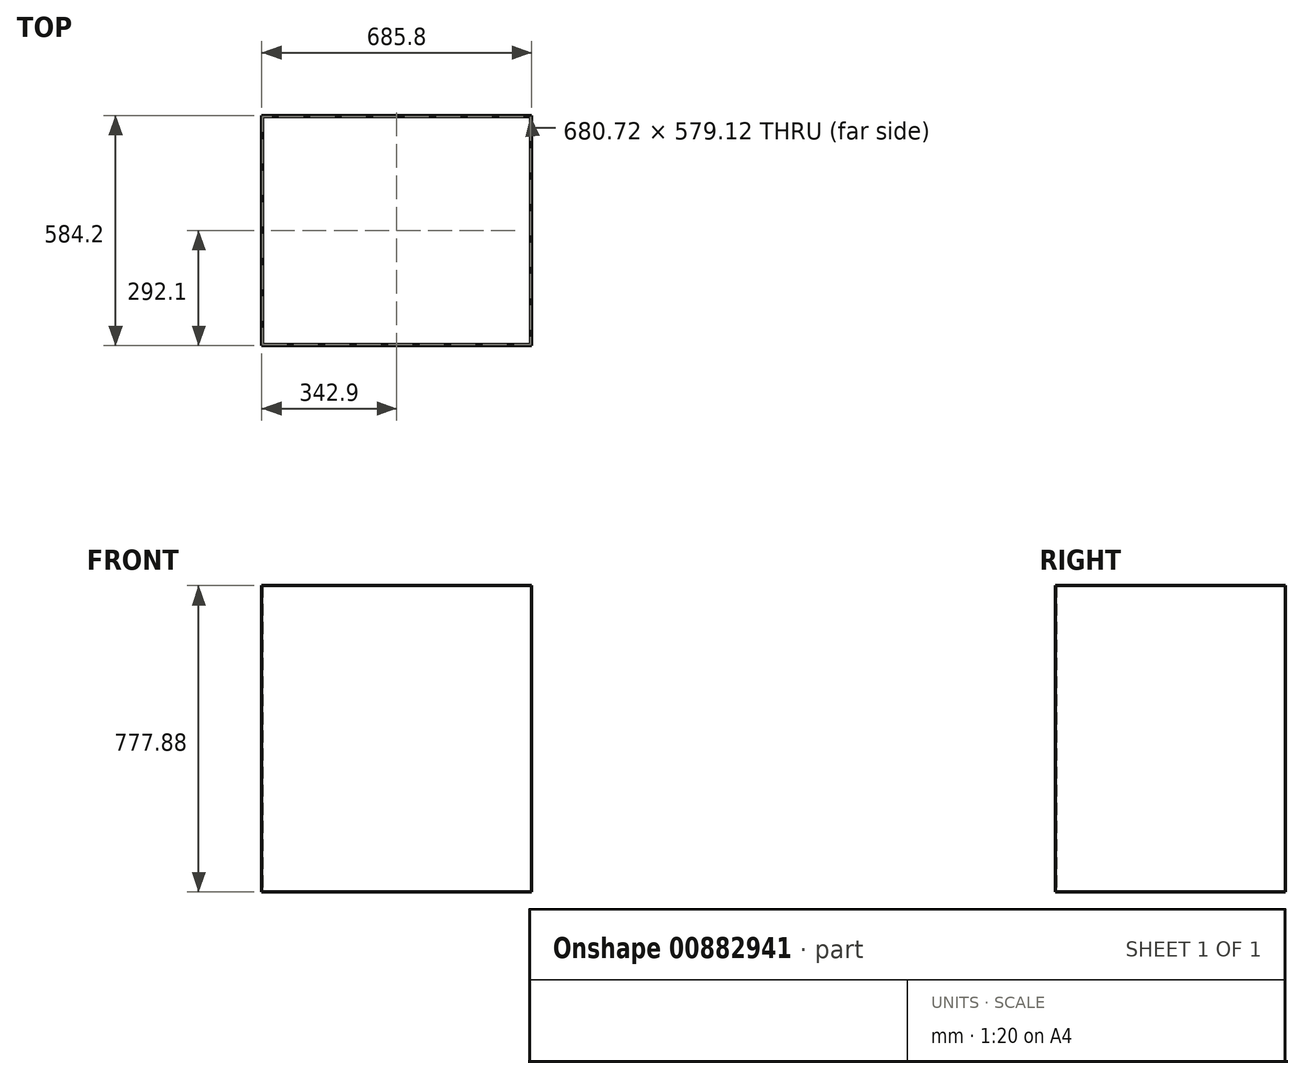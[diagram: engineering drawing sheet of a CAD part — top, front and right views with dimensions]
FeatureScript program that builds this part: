
annotation { "Feature Type Name" : "Feature", "Feature Type Description" : "" }
export const myFeature = defineFeature(function(context is Context, id is Id, definition is map)
    precondition{}
    {
        {
            var Q0;
            Q0=qCreatedBy(makeId("Top.planeOp"),FACE);
            var sketch = newSketch(context, id + "F0", { "sketchPlane" : qUnion([Q0])});
            skLineSegment(sketch, "E0.bottom", {"start": v(-342.9, 292.1) * mm, "end": v(342.9, 292.1) * mm});
            skLineSegment(sketch, "E0.top", {"start": v(-342.9, -292.1) * mm, "end": v(342.9, -292.1) * mm});
            skLineSegment(sketch, "E0.left", {"start": v(-342.9, 292.1) * mm, "end": v(-342.9, -292.1) * mm});
            skLineSegment(sketch, "E0.right", {"start": v(342.9, 292.1) * mm, "end": v(342.9, -292.1) * mm});
            skPoint(sketch, "E0.middle", {"position": v(0, 0) * mm});
            skSolve(sketch);
        }
        {
            var Q0;
            Q0=makeQuery(id+"F0.imprint","IMPRINT",FACE,{"disambiguationData":[TD([[makeQuery(id+"F0.imprint","IMPRINT",EDGE,{"derivedFrom":sQuery(id+"F0.wireOp",EDGE,"E0.bottom")}),-1.0]])]});
            extrude(context, id + "F1", {"entities" : qUnion([Q0]), "depth" : 777.88 * mm, "offsetDistance" : 25.4 * mm});
        }
        {
            var Q0;
            Q0=makeQuery(id+"F1.opExtrude","CAP_FACE",FACE,{"disambiguationData":[OSD([sQuery(id+"F0.wireOp",EDGE,"E0.bottom"),sQuery(id+"F0.wireOp",EDGE,"E0.top"),sQuery(id+"F0.wireOp",EDGE,"E0.left"),sQuery(id+"F0.wireOp",EDGE,"E0.right")])],"isStart":true});
            var Q1;
            Q1=makeQuery(id+"F1.opExtrude","CAP_FACE",FACE,{"disambiguationData":[OSD([sQuery(id+"F0.wireOp",EDGE,"E0.bottom"),sQuery(id+"F0.wireOp",EDGE,"E0.top"),sQuery(id+"F0.wireOp",EDGE,"E0.left"),sQuery(id+"F0.wireOp",EDGE,"E0.right")])],"isStart":false});
            shell(context, id + "F2", {"entities" : qUnion([Q0, Q1]), "thickness" : 2.54 * mm});
        }
    });
